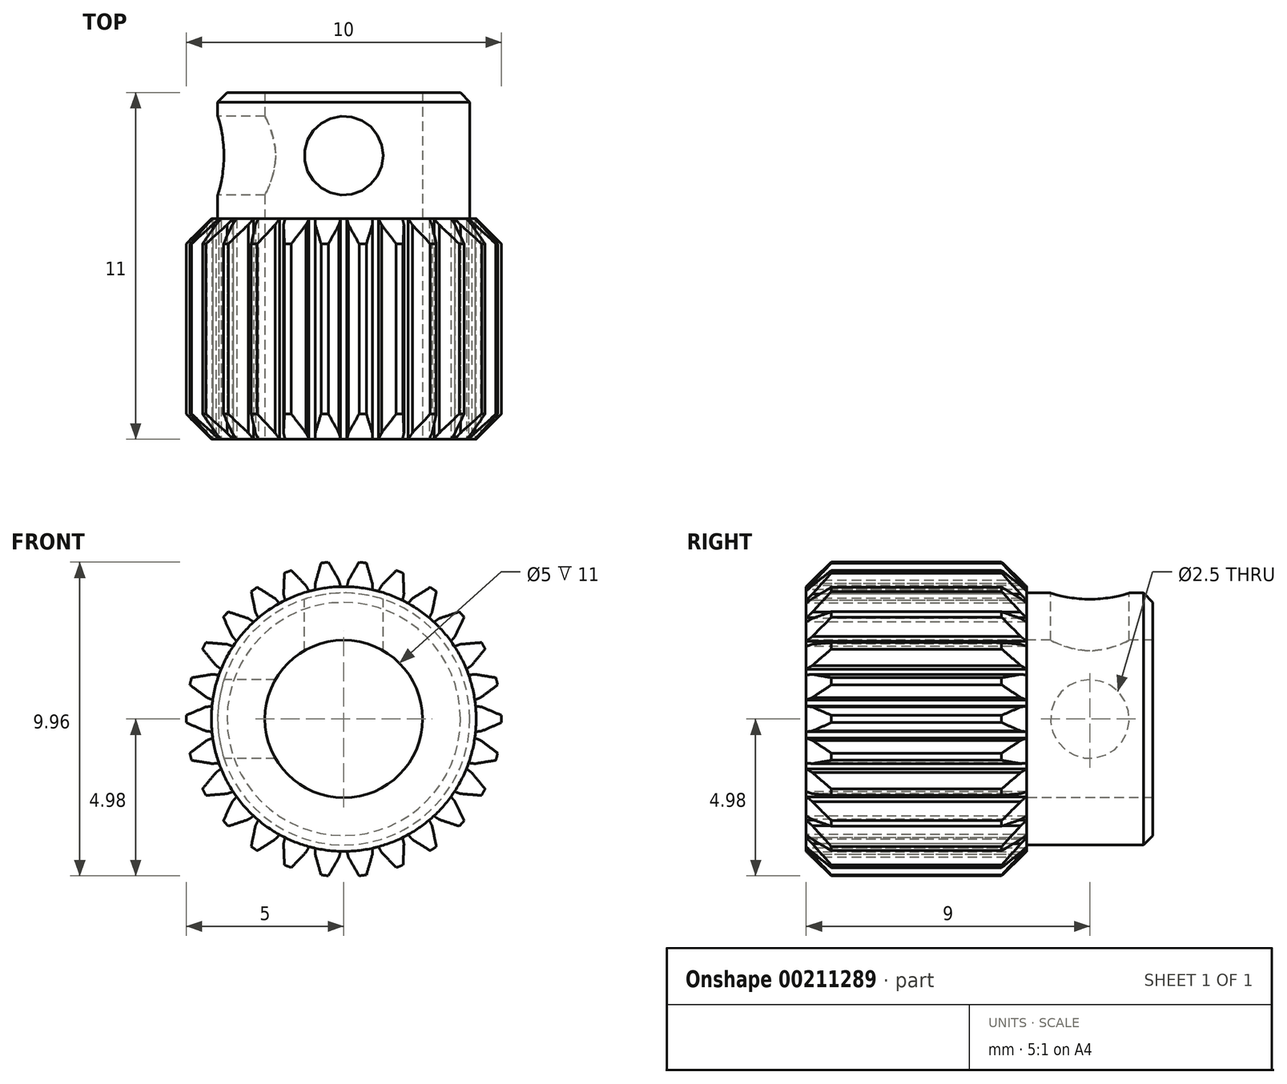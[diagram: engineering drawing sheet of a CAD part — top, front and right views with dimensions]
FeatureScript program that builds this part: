
annotation { "Feature Type Name" : "Feature", "Feature Type Description" : "" }
export const myFeature = defineFeature(function(context is Context, id is Id, definition is map)
    precondition{}
    {
        {
            var Q0;
            Q0=qCreatedBy(makeId("Right.planeOp"),FACE);
            var sketch = newSketch(context, id + "F0", { "sketchPlane" : qUnion([Q0])});
            skLineSegment(sketch, "E0", {"start": v(-5.5, 0) * mm, "end": v(5.5, 0) * mm, "construction": true});
            skLineSegment(sketch, "E1", {"start": v(-5.5, 2.5) * mm, "end": v(5.5, 2.5) * mm});
            skLineSegment(sketch, "E2", {"start": v(5.5, 2.5) * mm, "end": v(5.5, 4) * mm});
            skLineSegment(sketch, "E3", {"start": v(5.5, 4) * mm, "end": v(1.5, 4) * mm});
            skLineSegment(sketch, "E4", {"start": v(1.5, 4) * mm, "end": v(1.5, 5) * mm});
            skLineSegment(sketch, "E5", {"start": v(1.5, 5) * mm, "end": v(-5.5, 5) * mm});
            skLineSegment(sketch, "E6", {"start": v(-5.5, 5) * mm, "end": v(-5.5, 2.5) * mm});
            skSolve(sketch);
        }
        {
            var Q0;
            Q0=makeQuery(id+"F0.imprint","IMPRINT",FACE,{"disambiguationData":[TD([[makeQuery(id+"F0.imprint","IMPRINT",EDGE,{"derivedFrom":sQuery(id+"F0.wireOp",EDGE,"E1")}),1.0]])]});
            var Q1;
            Q1=sQuery(id+"F0.wireOp",EDGE,"E0");
            revolve(context, id + "F1", {"entities" : qUnion([Q0]), "axis" : qUnion([Q1]), "revolveType" : RevolveType.FULL});
        }
        {
            var Q0;
            Q0=makeQuery(id+"F1.opRevolve","SWEPT_EDGE",EDGE,{"disambiguationData":[OSD([sQuery(id+"F0.wireOp",EDGE,"E4"),sQuery(id+"F0.wireOp",EDGE,"E5")])]});
            var Q1;
            Q1=makeQuery(id+"F1.opRevolve","SWEPT_EDGE",EDGE,{"disambiguationData":[OSD([sQuery(id+"F0.wireOp",EDGE,"E5"),sQuery(id+"F0.wireOp",EDGE,"E6")])]});
            chamfer(context, id + "F2", {"entities" : qUnion([Q0, Q1]), "width" : .8 * mm, "tangentPropagation" : true});
        }
        {
            var Q0;
            Q0=makeQuery(id+"F1.opRevolve","SWEPT_FACE",FACE,{"disambiguationData":[OSD([sQuery(id+"F0.wireOp",EDGE,"E6")])]});
            var sketch = newSketch(context, id + "F3", { "sketchPlane" : qUnion([Q0])});
            skLineSegment(sketch, "E7", {"start": v(0, 0) * mm, "end": v(0, 5) * mm, "construction": true});
            skLineSegment(sketch, "E8", {"start": v(0, 4.2) * mm, "end": v(-0.1, 4.2) * mm});
            skLineSegment(sketch, "E9", {"start": v(-0.1, 4.2) * mm, "end": v(-0.15, 4.4) * mm});
            skLineSegment(sketch, "E10", {"start": v(-0.15, 4.4) * mm, "end": v(-0.5, 5) * mm});
            skLineSegment(sketch, "E11", {"start": v(0, 5) * mm, "end": v(-0.5, 5) * mm});
            skLineSegment(sketch, "E12.MirrorCS", {"start": v(0, 5) * mm, "end": v(0.5, 5) * mm});
            skLineSegment(sketch, "E13.MirrorCS", {"start": v(0.15, 4.4) * mm, "end": v(0.5, 5) * mm});
            skLineSegment(sketch, "E14.MirrorCS", {"start": v(0, 4.2) * mm, "end": v(0.1, 4.2) * mm});
            skLineSegment(sketch, "E15.MirrorCS", {"start": v(0.1, 4.2) * mm, "end": v(0.15, 4.4) * mm});
            skLineSegment(sketch, "E16.1.0", {"start": v(-0.9, 4.3) * mm, "end": v(-0.71, 4.97) * mm});
            skLineSegment(sketch, "E16.1.1", {"start": v(-1.2, 4.85) * mm, "end": v(-0.71, 4.97) * mm});
            skLineSegment(sketch, "E16.1.2", {"start": v(-1.2, 4.85) * mm, "end": v(-1.68, 4.74) * mm});
            skLineSegment(sketch, "E16.1.3", {"start": v(-1.2, 4.23) * mm, "end": v(-1.68, 4.74) * mm});
            skLineSegment(sketch, "E16.1.4", {"start": v(-1.1, 4.05) * mm, "end": v(-1.2, 4.23) * mm});
            skLineSegment(sketch, "E16.1.5", {"start": v(-0.9, 4.1) * mm, "end": v(-0.9, 4.3) * mm});
            skLineSegment(sketch, "E16.1.6", {"start": v(-1, 4.08) * mm, "end": v(-1.1, 4.05) * mm});
            skLineSegment(sketch, "E16.1.7", {"start": v(-1, 4.08) * mm, "end": v(-0.9, 4.1) * mm});
            skLineSegment(sketch, "E16.2.0", {"start": v(-1.9, 3.96) * mm, "end": v(-1.88, 4.66) * mm});
            skLineSegment(sketch, "E16.2.1", {"start": v(-2.32, 4.43) * mm, "end": v(-1.88, 4.66) * mm});
            skLineSegment(sketch, "E16.2.2", {"start": v(-2.32, 4.43) * mm, "end": v(-2.77, 4.2) * mm});
            skLineSegment(sketch, "E16.2.3", {"start": v(-2.17, 3.82) * mm, "end": v(-2.77, 4.2) * mm});
            skLineSegment(sketch, "E16.2.4", {"start": v(-2.04, 3.67) * mm, "end": v(-2.17, 3.82) * mm});
            skLineSegment(sketch, "E16.2.5", {"start": v(-1.86, 3.77) * mm, "end": v(-1.9, 3.96) * mm});
            skLineSegment(sketch, "E16.2.6", {"start": v(-1.95, 3.72) * mm, "end": v(-2.04, 3.67) * mm});
            skLineSegment(sketch, "E16.2.7", {"start": v(-1.95, 3.72) * mm, "end": v(-1.86, 3.77) * mm});
            skLineSegment(sketch, "E16.3.0", {"start": v(-2.8, 3.39) * mm, "end": v(-2.94, 4.07) * mm});
            skLineSegment(sketch, "E16.3.1", {"start": v(-3.32, 3.74) * mm, "end": v(-2.94, 4.07) * mm});
            skLineSegment(sketch, "E16.3.2", {"start": v(-3.32, 3.74) * mm, "end": v(-3.69, 3.41) * mm});
            skLineSegment(sketch, "E16.3.3", {"start": v(-3.03, 3.19) * mm, "end": v(-3.69, 3.41) * mm});
            skLineSegment(sketch, "E16.3.4", {"start": v(-2.86, 3.08) * mm, "end": v(-3.03, 3.19) * mm});
            skLineSegment(sketch, "E16.3.5", {"start": v(-2.71, 3.21) * mm, "end": v(-2.8, 3.39) * mm});
            skLineSegment(sketch, "E16.3.6", {"start": v(-2.79, 3.14) * mm, "end": v(-2.86, 3.08) * mm});
            skLineSegment(sketch, "E16.3.7", {"start": v(-2.79, 3.14) * mm, "end": v(-2.71, 3.21) * mm});
            skLineSegment(sketch, "E16.4.0", {"start": v(-3.53, 2.62) * mm, "end": v(-3.83, 3.25) * mm});
            skLineSegment(sketch, "E16.4.1", {"start": v(-4.11, 2.84) * mm, "end": v(-3.83, 3.25) * mm});
            skLineSegment(sketch, "E16.4.2", {"start": v(-4.11, 2.84) * mm, "end": v(-4.4, 2.43) * mm});
            skLineSegment(sketch, "E16.4.3", {"start": v(-3.7, 2.37) * mm, "end": v(-4.4, 2.43) * mm});
            skLineSegment(sketch, "E16.4.4", {"start": v(-3.51, 2.3) * mm, "end": v(-3.7, 2.37) * mm});
            skLineSegment(sketch, "E16.4.5", {"start": v(-3.4, 2.47) * mm, "end": v(-3.53, 2.62) * mm});
            skLineSegment(sketch, "E16.4.6", {"start": v(-3.46, 2.39) * mm, "end": v(-3.51, 2.3) * mm});
            skLineSegment(sketch, "E16.4.7", {"start": v(-3.46, 2.39) * mm, "end": v(-3.4, 2.47) * mm});
            skLineSegment(sketch, "E16.5.0", {"start": v(-4.06, 1.7) * mm, "end": v(-4.5, 2.24) * mm});
            skLineSegment(sketch, "E16.5.1", {"start": v(-4.68, 1.77) * mm, "end": v(-4.5, 2.24) * mm});
            skLineSegment(sketch, "E16.5.2", {"start": v(-4.68, 1.77) * mm, "end": v(-4.85, 1.3) * mm});
            skLineSegment(sketch, "E16.5.3", {"start": v(-4.16, 1.42) * mm, "end": v(-4.85, 1.3) * mm});
            skLineSegment(sketch, "E16.5.4", {"start": v(-3.96, 1.4) * mm, "end": v(-4.16, 1.42) * mm});
            skLineSegment(sketch, "E16.5.5", {"start": v(-3.9, 1.58) * mm, "end": v(-4.06, 1.7) * mm});
            skLineSegment(sketch, "E16.5.6", {"start": v(-3.93, 1.49) * mm, "end": v(-3.96, 1.4) * mm});
            skLineSegment(sketch, "E16.5.7", {"start": v(-3.93, 1.49) * mm, "end": v(-3.9, 1.58) * mm});
            skLineSegment(sketch, "E16.6.0", {"start": v(-4.34, 0.68) * mm, "end": v(-4.9, 1.1) * mm});
            skLineSegment(sketch, "E16.6.1", {"start": v(-4.96, 0.6) * mm, "end": v(-4.9, 1.1) * mm});
            skLineSegment(sketch, "E16.6.2", {"start": v(-4.96, 0.6) * mm, "end": v(-5.02, 0.1) * mm});
            skLineSegment(sketch, "E16.6.3", {"start": v(-4.38, 0.38) * mm, "end": v(-5.02, 0.1) * mm});
            skLineSegment(sketch, "E16.6.4", {"start": v(-4.18, 0.4) * mm, "end": v(-4.38, 0.38) * mm});
            skLineSegment(sketch, "E16.6.5", {"start": v(-4.16, 0.6) * mm, "end": v(-4.34, 0.68) * mm});
            skLineSegment(sketch, "E16.6.6", {"start": v(-4.17, 0.5) * mm, "end": v(-4.18, 0.4) * mm});
            skLineSegment(sketch, "E16.6.7", {"start": v(-4.17, 0.5) * mm, "end": v(-4.16, 0.6) * mm});
            skLineSegment(sketch, "E16.7.0", {"start": v(-4.38, -0.38) * mm, "end": v(-5.02, -0.1) * mm});
            skLineSegment(sketch, "E16.7.1", {"start": v(-4.96, -0.6) * mm, "end": v(-5.02, -0.1) * mm});
            skLineSegment(sketch, "E16.7.2", {"start": v(-4.96, -0.6) * mm, "end": v(-4.9, -1.1) * mm});
            skLineSegment(sketch, "E16.7.3", {"start": v(-4.34, -0.68) * mm, "end": v(-4.9, -1.1) * mm});
            skLineSegment(sketch, "E16.7.4", {"start": v(-4.16, -0.6) * mm, "end": v(-4.34, -0.68) * mm});
            skLineSegment(sketch, "E16.7.5", {"start": v(-4.18, -0.4) * mm, "end": v(-4.38, -0.38) * mm});
            skLineSegment(sketch, "E16.7.6", {"start": v(-4.17, -0.5) * mm, "end": v(-4.16, -0.6) * mm});
            skLineSegment(sketch, "E16.7.7", {"start": v(-4.17, -0.5) * mm, "end": v(-4.18, -0.4) * mm});
            skLineSegment(sketch, "E16.8.0", {"start": v(-4.16, -1.42) * mm, "end": v(-4.85, -1.3) * mm});
            skLineSegment(sketch, "E16.8.1", {"start": v(-4.68, -1.77) * mm, "end": v(-4.85, -1.3) * mm});
            skLineSegment(sketch, "E16.8.2", {"start": v(-4.68, -1.77) * mm, "end": v(-4.5, -2.24) * mm});
            skLineSegment(sketch, "E16.8.3", {"start": v(-4.06, -1.7) * mm, "end": v(-4.5, -2.24) * mm});
            skLineSegment(sketch, "E16.8.4", {"start": v(-3.9, -1.58) * mm, "end": v(-4.06, -1.7) * mm});
            skLineSegment(sketch, "E16.8.5", {"start": v(-3.96, -1.4) * mm, "end": v(-4.16, -1.42) * mm});
            skLineSegment(sketch, "E16.8.6", {"start": v(-3.93, -1.49) * mm, "end": v(-3.9, -1.58) * mm});
            skLineSegment(sketch, "E16.8.7", {"start": v(-3.93, -1.49) * mm, "end": v(-3.96, -1.4) * mm});
            skLineSegment(sketch, "E16.9.0", {"start": v(-3.7, -2.37) * mm, "end": v(-4.4, -2.43) * mm});
            skLineSegment(sketch, "E16.9.1", {"start": v(-4.11, -2.84) * mm, "end": v(-4.4, -2.43) * mm});
            skLineSegment(sketch, "E16.9.2", {"start": v(-4.11, -2.84) * mm, "end": v(-3.83, -3.25) * mm});
            skLineSegment(sketch, "E16.9.3", {"start": v(-3.53, -2.62) * mm, "end": v(-3.83, -3.25) * mm});
            skLineSegment(sketch, "E16.9.4", {"start": v(-3.4, -2.47) * mm, "end": v(-3.53, -2.62) * mm});
            skLineSegment(sketch, "E16.9.5", {"start": v(-3.51, -2.3) * mm, "end": v(-3.7, -2.37) * mm});
            skLineSegment(sketch, "E16.9.6", {"start": v(-3.46, -2.39) * mm, "end": v(-3.4, -2.47) * mm});
            skLineSegment(sketch, "E16.9.7", {"start": v(-3.46, -2.39) * mm, "end": v(-3.51, -2.3) * mm});
            skLineSegment(sketch, "E16.10.0", {"start": v(-3.03, -3.19) * mm, "end": v(-3.69, -3.41) * mm});
            skLineSegment(sketch, "E16.10.1", {"start": v(-3.32, -3.74) * mm, "end": v(-3.69, -3.41) * mm});
            skLineSegment(sketch, "E16.10.2", {"start": v(-3.32, -3.74) * mm, "end": v(-2.94, -4.07) * mm});
            skLineSegment(sketch, "E16.10.3", {"start": v(-2.8, -3.39) * mm, "end": v(-2.94, -4.07) * mm});
            skLineSegment(sketch, "E16.10.4", {"start": v(-2.71, -3.21) * mm, "end": v(-2.8, -3.39) * mm});
            skLineSegment(sketch, "E16.10.5", {"start": v(-2.86, -3.08) * mm, "end": v(-3.03, -3.19) * mm});
            skLineSegment(sketch, "E16.10.6", {"start": v(-2.79, -3.14) * mm, "end": v(-2.71, -3.21) * mm});
            skLineSegment(sketch, "E16.10.7", {"start": v(-2.79, -3.14) * mm, "end": v(-2.86, -3.08) * mm});
            skLineSegment(sketch, "E16.11.0", {"start": v(-2.17, -3.82) * mm, "end": v(-2.77, -4.2) * mm});
            skLineSegment(sketch, "E16.11.1", {"start": v(-2.32, -4.43) * mm, "end": v(-2.77, -4.2) * mm});
            skLineSegment(sketch, "E16.11.2", {"start": v(-2.32, -4.43) * mm, "end": v(-1.88, -4.66) * mm});
            skLineSegment(sketch, "E16.11.3", {"start": v(-1.9, -3.96) * mm, "end": v(-1.88, -4.66) * mm});
            skLineSegment(sketch, "E16.11.4", {"start": v(-1.86, -3.77) * mm, "end": v(-1.9, -3.96) * mm});
            skLineSegment(sketch, "E16.11.5", {"start": v(-2.04, -3.67) * mm, "end": v(-2.17, -3.82) * mm});
            skLineSegment(sketch, "E16.11.6", {"start": v(-1.95, -3.72) * mm, "end": v(-1.86, -3.77) * mm});
            skLineSegment(sketch, "E16.11.7", {"start": v(-1.95, -3.72) * mm, "end": v(-2.04, -3.67) * mm});
            skLineSegment(sketch, "E16.12.0", {"start": v(-1.2, -4.23) * mm, "end": v(-1.68, -4.74) * mm});
            skLineSegment(sketch, "E16.12.1", {"start": v(-1.2, -4.85) * mm, "end": v(-1.68, -4.74) * mm});
            skLineSegment(sketch, "E16.12.2", {"start": v(-1.2, -4.85) * mm, "end": v(-0.71, -4.97) * mm});
            skLineSegment(sketch, "E16.12.3", {"start": v(-0.9, -4.3) * mm, "end": v(-0.71, -4.97) * mm});
            skLineSegment(sketch, "E16.12.4", {"start": v(-0.9, -4.1) * mm, "end": v(-0.9, -4.3) * mm});
            skLineSegment(sketch, "E16.12.5", {"start": v(-1.1, -4.05) * mm, "end": v(-1.2, -4.23) * mm});
            skLineSegment(sketch, "E16.12.6", {"start": v(-1, -4.08) * mm, "end": v(-0.9, -4.1) * mm});
            skLineSegment(sketch, "E16.12.7", {"start": v(-1, -4.08) * mm, "end": v(-1.1, -4.05) * mm});
            skLineSegment(sketch, "E16.13.0", {"start": v(-0.15, -4.4) * mm, "end": v(-0.5, -5) * mm});
            skLineSegment(sketch, "E16.13.1", {"start": v(0, -5) * mm, "end": v(-0.5, -5) * mm});
            skLineSegment(sketch, "E16.13.2", {"start": v(0, -5) * mm, "end": v(0.5, -5) * mm});
            skLineSegment(sketch, "E16.13.3", {"start": v(0.15, -4.4) * mm, "end": v(0.5, -5) * mm});
            skLineSegment(sketch, "E16.13.4", {"start": v(0.1, -4.2) * mm, "end": v(0.15, -4.4) * mm});
            skLineSegment(sketch, "E16.13.5", {"start": v(-0.1, -4.2) * mm, "end": v(-0.15, -4.4) * mm});
            skLineSegment(sketch, "E16.13.6", {"start": v(0, -4.2) * mm, "end": v(0.1, -4.2) * mm});
            skLineSegment(sketch, "E16.13.7", {"start": v(0, -4.2) * mm, "end": v(-0.1, -4.2) * mm});
            skLineSegment(sketch, "E16.14.0", {"start": v(0.9, -4.3) * mm, "end": v(0.71, -4.97) * mm});
            skLineSegment(sketch, "E16.14.1", {"start": v(1.2, -4.85) * mm, "end": v(0.71, -4.97) * mm});
            skLineSegment(sketch, "E16.14.2", {"start": v(1.2, -4.85) * mm, "end": v(1.68, -4.74) * mm});
            skLineSegment(sketch, "E16.14.3", {"start": v(1.2, -4.23) * mm, "end": v(1.68, -4.74) * mm});
            skLineSegment(sketch, "E16.14.4", {"start": v(1.1, -4.05) * mm, "end": v(1.2, -4.23) * mm});
            skLineSegment(sketch, "E16.14.5", {"start": v(0.9, -4.1) * mm, "end": v(0.9, -4.3) * mm});
            skLineSegment(sketch, "E16.14.6", {"start": v(1, -4.08) * mm, "end": v(1.1, -4.05) * mm});
            skLineSegment(sketch, "E16.14.7", {"start": v(1, -4.08) * mm, "end": v(0.9, -4.1) * mm});
            skLineSegment(sketch, "E16.15.0", {"start": v(1.9, -3.96) * mm, "end": v(1.88, -4.66) * mm});
            skLineSegment(sketch, "E16.15.1", {"start": v(2.32, -4.43) * mm, "end": v(1.88, -4.66) * mm});
            skLineSegment(sketch, "E16.15.2", {"start": v(2.32, -4.43) * mm, "end": v(2.77, -4.2) * mm});
            skLineSegment(sketch, "E16.15.3", {"start": v(2.17, -3.82) * mm, "end": v(2.77, -4.2) * mm});
            skLineSegment(sketch, "E16.15.4", {"start": v(2.04, -3.67) * mm, "end": v(2.17, -3.82) * mm});
            skLineSegment(sketch, "E16.15.5", {"start": v(1.86, -3.77) * mm, "end": v(1.9, -3.96) * mm});
            skLineSegment(sketch, "E16.15.6", {"start": v(1.95, -3.72) * mm, "end": v(2.04, -3.67) * mm});
            skLineSegment(sketch, "E16.15.7", {"start": v(1.95, -3.72) * mm, "end": v(1.86, -3.77) * mm});
            skLineSegment(sketch, "E16.16.0", {"start": v(2.8, -3.39) * mm, "end": v(2.94, -4.07) * mm});
            skLineSegment(sketch, "E16.16.1", {"start": v(3.32, -3.74) * mm, "end": v(2.94, -4.07) * mm});
            skLineSegment(sketch, "E16.16.2", {"start": v(3.32, -3.74) * mm, "end": v(3.69, -3.41) * mm});
            skLineSegment(sketch, "E16.16.3", {"start": v(3.03, -3.19) * mm, "end": v(3.69, -3.41) * mm});
            skLineSegment(sketch, "E16.16.4", {"start": v(2.86, -3.08) * mm, "end": v(3.03, -3.19) * mm});
            skLineSegment(sketch, "E16.16.5", {"start": v(2.71, -3.21) * mm, "end": v(2.8, -3.39) * mm});
            skLineSegment(sketch, "E16.16.6", {"start": v(2.79, -3.14) * mm, "end": v(2.86, -3.08) * mm});
            skLineSegment(sketch, "E16.16.7", {"start": v(2.79, -3.14) * mm, "end": v(2.71, -3.21) * mm});
            skLineSegment(sketch, "E16.17.0", {"start": v(3.53, -2.62) * mm, "end": v(3.83, -3.25) * mm});
            skLineSegment(sketch, "E16.17.1", {"start": v(4.11, -2.84) * mm, "end": v(3.83, -3.25) * mm});
            skLineSegment(sketch, "E16.17.2", {"start": v(4.11, -2.84) * mm, "end": v(4.4, -2.43) * mm});
            skLineSegment(sketch, "E16.17.3", {"start": v(3.7, -2.37) * mm, "end": v(4.4, -2.43) * mm});
            skLineSegment(sketch, "E16.17.4", {"start": v(3.51, -2.3) * mm, "end": v(3.7, -2.37) * mm});
            skLineSegment(sketch, "E16.17.5", {"start": v(3.4, -2.47) * mm, "end": v(3.53, -2.62) * mm});
            skLineSegment(sketch, "E16.17.6", {"start": v(3.46, -2.39) * mm, "end": v(3.51, -2.3) * mm});
            skLineSegment(sketch, "E16.17.7", {"start": v(3.46, -2.39) * mm, "end": v(3.4, -2.47) * mm});
            skLineSegment(sketch, "E16.18.0", {"start": v(4.06, -1.7) * mm, "end": v(4.5, -2.24) * mm});
            skLineSegment(sketch, "E16.18.1", {"start": v(4.68, -1.77) * mm, "end": v(4.5, -2.24) * mm});
            skLineSegment(sketch, "E16.18.2", {"start": v(4.68, -1.77) * mm, "end": v(4.85, -1.3) * mm});
            skLineSegment(sketch, "E16.18.3", {"start": v(4.16, -1.42) * mm, "end": v(4.85, -1.3) * mm});
            skLineSegment(sketch, "E16.18.4", {"start": v(3.96, -1.4) * mm, "end": v(4.16, -1.42) * mm});
            skLineSegment(sketch, "E16.18.5", {"start": v(3.9, -1.58) * mm, "end": v(4.06, -1.7) * mm});
            skLineSegment(sketch, "E16.18.6", {"start": v(3.93, -1.49) * mm, "end": v(3.96, -1.4) * mm});
            skLineSegment(sketch, "E16.18.7", {"start": v(3.93, -1.49) * mm, "end": v(3.9, -1.58) * mm});
            skLineSegment(sketch, "E16.19.0", {"start": v(4.34, -0.68) * mm, "end": v(4.9, -1.1) * mm});
            skLineSegment(sketch, "E16.19.1", {"start": v(4.96, -0.6) * mm, "end": v(4.9, -1.1) * mm});
            skLineSegment(sketch, "E16.19.2", {"start": v(4.96, -0.6) * mm, "end": v(5.02, -0.1) * mm});
            skLineSegment(sketch, "E16.19.3", {"start": v(4.38, -0.38) * mm, "end": v(5.02, -0.1) * mm});
            skLineSegment(sketch, "E16.19.4", {"start": v(4.18, -0.4) * mm, "end": v(4.38, -0.38) * mm});
            skLineSegment(sketch, "E16.19.5", {"start": v(4.16, -0.6) * mm, "end": v(4.34, -0.68) * mm});
            skLineSegment(sketch, "E16.19.6", {"start": v(4.17, -0.5) * mm, "end": v(4.18, -0.4) * mm});
            skLineSegment(sketch, "E16.19.7", {"start": v(4.17, -0.5) * mm, "end": v(4.16, -0.6) * mm});
            skLineSegment(sketch, "E16.20.0", {"start": v(4.38, 0.38) * mm, "end": v(5.02, 0.1) * mm});
            skLineSegment(sketch, "E16.20.1", {"start": v(4.96, 0.6) * mm, "end": v(5.02, 0.1) * mm});
            skLineSegment(sketch, "E16.20.2", {"start": v(4.96, 0.6) * mm, "end": v(4.9, 1.1) * mm});
            skLineSegment(sketch, "E16.20.3", {"start": v(4.34, 0.68) * mm, "end": v(4.9, 1.1) * mm});
            skLineSegment(sketch, "E16.20.4", {"start": v(4.16, 0.6) * mm, "end": v(4.34, 0.68) * mm});
            skLineSegment(sketch, "E16.20.5", {"start": v(4.18, 0.4) * mm, "end": v(4.38, 0.38) * mm});
            skLineSegment(sketch, "E16.20.6", {"start": v(4.17, 0.5) * mm, "end": v(4.16, 0.6) * mm});
            skLineSegment(sketch, "E16.20.7", {"start": v(4.17, 0.5) * mm, "end": v(4.18, 0.4) * mm});
            skLineSegment(sketch, "E16.21.0", {"start": v(4.16, 1.42) * mm, "end": v(4.85, 1.3) * mm});
            skLineSegment(sketch, "E16.21.1", {"start": v(4.68, 1.77) * mm, "end": v(4.85, 1.3) * mm});
            skLineSegment(sketch, "E16.21.2", {"start": v(4.68, 1.77) * mm, "end": v(4.5, 2.24) * mm});
            skLineSegment(sketch, "E16.21.3", {"start": v(4.06, 1.7) * mm, "end": v(4.5, 2.24) * mm});
            skLineSegment(sketch, "E16.21.4", {"start": v(3.9, 1.58) * mm, "end": v(4.06, 1.7) * mm});
            skLineSegment(sketch, "E16.21.5", {"start": v(3.96, 1.4) * mm, "end": v(4.16, 1.42) * mm});
            skLineSegment(sketch, "E16.21.6", {"start": v(3.93, 1.49) * mm, "end": v(3.9, 1.58) * mm});
            skLineSegment(sketch, "E16.21.7", {"start": v(3.93, 1.49) * mm, "end": v(3.96, 1.4) * mm});
            skLineSegment(sketch, "E16.22.0", {"start": v(3.7, 2.37) * mm, "end": v(4.4, 2.43) * mm});
            skLineSegment(sketch, "E16.22.1", {"start": v(4.11, 2.84) * mm, "end": v(4.4, 2.43) * mm});
            skLineSegment(sketch, "E16.22.2", {"start": v(4.11, 2.84) * mm, "end": v(3.83, 3.25) * mm});
            skLineSegment(sketch, "E16.22.3", {"start": v(3.53, 2.62) * mm, "end": v(3.83, 3.25) * mm});
            skLineSegment(sketch, "E16.22.4", {"start": v(3.4, 2.47) * mm, "end": v(3.53, 2.62) * mm});
            skLineSegment(sketch, "E16.22.5", {"start": v(3.51, 2.3) * mm, "end": v(3.7, 2.37) * mm});
            skLineSegment(sketch, "E16.22.6", {"start": v(3.46, 2.39) * mm, "end": v(3.4, 2.47) * mm});
            skLineSegment(sketch, "E16.22.7", {"start": v(3.46, 2.39) * mm, "end": v(3.51, 2.3) * mm});
            skLineSegment(sketch, "E16.23.0", {"start": v(3.03, 3.19) * mm, "end": v(3.69, 3.41) * mm});
            skLineSegment(sketch, "E16.23.1", {"start": v(3.32, 3.74) * mm, "end": v(3.69, 3.41) * mm});
            skLineSegment(sketch, "E16.23.2", {"start": v(3.32, 3.74) * mm, "end": v(2.94, 4.07) * mm});
            skLineSegment(sketch, "E16.23.3", {"start": v(2.8, 3.39) * mm, "end": v(2.94, 4.07) * mm});
            skLineSegment(sketch, "E16.23.4", {"start": v(2.71, 3.21) * mm, "end": v(2.8, 3.39) * mm});
            skLineSegment(sketch, "E16.23.5", {"start": v(2.86, 3.08) * mm, "end": v(3.03, 3.19) * mm});
            skLineSegment(sketch, "E16.23.6", {"start": v(2.79, 3.14) * mm, "end": v(2.71, 3.21) * mm});
            skLineSegment(sketch, "E16.23.7", {"start": v(2.79, 3.14) * mm, "end": v(2.86, 3.08) * mm});
            skLineSegment(sketch, "E16.24.0", {"start": v(2.17, 3.82) * mm, "end": v(2.77, 4.2) * mm});
            skLineSegment(sketch, "E16.24.1", {"start": v(2.32, 4.43) * mm, "end": v(2.77, 4.2) * mm});
            skLineSegment(sketch, "E16.24.2", {"start": v(2.32, 4.43) * mm, "end": v(1.88, 4.66) * mm});
            skLineSegment(sketch, "E16.24.3", {"start": v(1.9, 3.96) * mm, "end": v(1.88, 4.66) * mm});
            skLineSegment(sketch, "E16.24.4", {"start": v(1.86, 3.77) * mm, "end": v(1.9, 3.96) * mm});
            skLineSegment(sketch, "E16.24.5", {"start": v(2.04, 3.67) * mm, "end": v(2.17, 3.82) * mm});
            skLineSegment(sketch, "E16.24.6", {"start": v(1.95, 3.72) * mm, "end": v(1.86, 3.77) * mm});
            skLineSegment(sketch, "E16.24.7", {"start": v(1.95, 3.72) * mm, "end": v(2.04, 3.67) * mm});
            skLineSegment(sketch, "E16.25.0", {"start": v(1.2, 4.23) * mm, "end": v(1.68, 4.74) * mm});
            skLineSegment(sketch, "E16.25.1", {"start": v(1.2, 4.85) * mm, "end": v(1.68, 4.74) * mm});
            skLineSegment(sketch, "E16.25.2", {"start": v(1.2, 4.85) * mm, "end": v(0.71, 4.97) * mm});
            skLineSegment(sketch, "E16.25.3", {"start": v(0.9, 4.3) * mm, "end": v(0.71, 4.97) * mm});
            skLineSegment(sketch, "E16.25.4", {"start": v(0.9, 4.1) * mm, "end": v(0.9, 4.3) * mm});
            skLineSegment(sketch, "E16.25.5", {"start": v(1.1, 4.05) * mm, "end": v(1.2, 4.23) * mm});
            skLineSegment(sketch, "E16.25.6", {"start": v(1, 4.08) * mm, "end": v(0.9, 4.1) * mm});
            skLineSegment(sketch, "E16.25.7", {"start": v(1, 4.08) * mm, "end": v(1.1, 4.05) * mm});
            skPoint(sketch, "E16.center", {"position": v(0, 0) * mm});
            skSolve(sketch);
        }
        {
            var Q0;
            Q0 = qSketchRegion(id + "F3", true);
            extrude(context, id + "F4", {"entities" : qUnion([Q0]), "operationType" : NewBodyOperationType.REMOVE, "oppositeDirection" : true, "depth" : 10 * mm});
        }
        {
            var Q0;
            Q0=makeQuery(id+"F1.opRevolve","SWEPT_FACE",FACE,{"disambiguationData":[OSD([sQuery(id+"F0.wireOp",EDGE,"E2")])]});
            cPlane(context, id + "F5", {"entities" : qUnion([Q0]), "cplaneType" : CPlaneType.OFFSET, "offset" : 2 * mm, "oppositeDirection" : true, "width" : 150 * mm, "height" : 150 * mm});
        }
        {
            var Q0;
            Q0=qCreatedBy(id+"F5.planeOp",FACE);
            var sketch = newSketch(context, id + "F6", { "sketchPlane" : qUnion([Q0])});
            skLineSegment(sketch, "E17", {"start": v(0, 4) * mm, "end": v(0, 0) * mm});
            skLineSegment(sketch, "E18", {"start": v(0, 0) * mm, "end": v(4, 0) * mm});
            skSolve(sketch);
        }
        {
            var Q0;
            Q0=sQuery(id+"F6.wireOp",VERTEX,"E17.start");
            var Q1;
            Q1=sQuery(id+"F6.wireOp",EDGE,"E17");
            cPlane(context, id + "F7", {"entities" : qUnion([Q0, Q1]), "cplaneType" : CPlaneType.LINE_POINT, "offset" : 25 * mm, "width" : 150 * mm, "height" : 150 * mm});
        }
        {
            var Q0;
            Q0=qCreatedBy(id+"F7.planeOp",FACE);
            var sketch = newSketch(context, id + "F8", { "sketchPlane" : qUnion([Q0])});
            skPoint(sketch, "E19.0", {"position": v(0, -3.5) * mm});
            skSolve(sketch);
        }
        {
            var Q0;
            Q0=sQuery(id+"F6.wireOp",VERTEX,"E18.end");
            var Q1;
            Q1=sQuery(id+"F6.wireOp",EDGE,"E18");
            cPlane(context, id + "F9", {"entities" : qUnion([Q0, Q1]), "cplaneType" : CPlaneType.LINE_POINT, "offset" : 25 * mm, "width" : 150 * mm, "height" : 150 * mm});
        }
        {
            var Q0;
            Q0=qCreatedBy(id+"F9.planeOp",FACE);
            var sketch = newSketch(context, id + "F10", { "sketchPlane" : qUnion([Q0])});
            skPoint(sketch, "E20.0", {"position": v(-3.5, 0) * mm});
            skSolve(sketch);
        }
        {
            var Q0;
            Q0=sQuery(id+"F8.wireOp",VERTEX,"E19.0");
            var Q1;
            Q1=makeQuery(id+"F1.opRevolve","SWEPT_BODY",BODY,{"disambiguationData":[OSD([sQuery(id+"F0.wireOp",EDGE,"E1"),sQuery(id+"F0.wireOp",EDGE,"E2"),sQuery(id+"F0.wireOp",EDGE,"E3"),sQuery(id+"F0.wireOp",EDGE,"E4"),sQuery(id+"F0.wireOp",EDGE,"E5"),sQuery(id+"F0.wireOp",EDGE,"E6")])]});
            hole(context, id + "F11", {"style" : HoleStyle.SIMPLE, "endStyle" : HoleEndStyle.BLIND, "oppositeDirection" : true, "holeDiameter" : 2.5 * mm, "holeDepth" : 4 * mm, "locations" : qUnion([Q0]), "scope" : qUnion([Q1])});
        }
        {
            var Q0;
            Q0=sQuery(id+"F10.wireOp",VERTEX,"E20.0");
            var Q1;
            Q1=makeQuery(id+"F1.opRevolve","SWEPT_BODY",BODY,{"disambiguationData":[OSD([sQuery(id+"F0.wireOp",EDGE,"E1"),sQuery(id+"F0.wireOp",EDGE,"E2"),sQuery(id+"F0.wireOp",EDGE,"E3"),sQuery(id+"F0.wireOp",EDGE,"E4"),sQuery(id+"F0.wireOp",EDGE,"E5"),sQuery(id+"F0.wireOp",EDGE,"E6")])]});
            hole(context, id + "F12", {"style" : HoleStyle.SIMPLE, "endStyle" : HoleEndStyle.BLIND, "holeDiameter" : 2.5 * mm, "holeDepth" : 4 * mm, "locations" : qUnion([Q0]), "scope" : qUnion([Q1])});
        }
        {
            var Q0;
            Q0=makeQuery(id+"F1.opRevolve","SWEPT_EDGE",EDGE,{"disambiguationData":[OSD([sQuery(id+"F0.wireOp",EDGE,"E2"),sQuery(id+"F0.wireOp",EDGE,"E3")])]});
            chamfer(context, id + "F13", {"entities" : qUnion([Q0]), "width" : .3 * mm, "tangentPropagation" : true});
        }
    });
